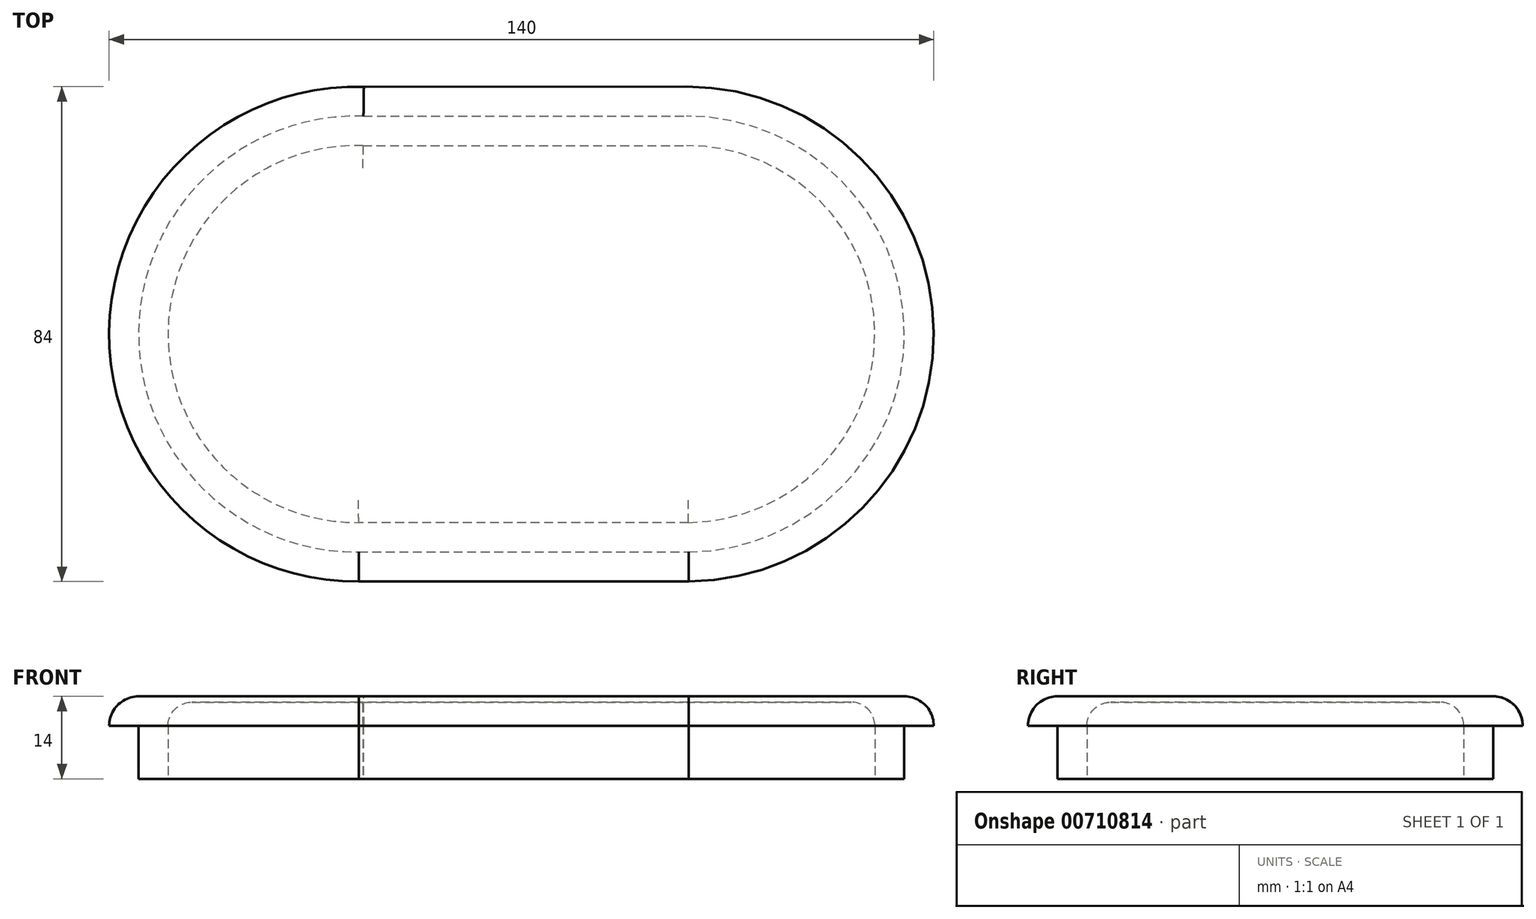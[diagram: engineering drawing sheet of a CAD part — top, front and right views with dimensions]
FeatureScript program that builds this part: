
annotation { "Feature Type Name" : "Feature", "Feature Type Description" : "" }
export const myFeature = defineFeature(function(context is Context, id is Id, definition is map)
    precondition{}
    {
        {
            var Q0;
            Q0=qCreatedBy(makeId("Top.planeOp"),FACE);
            var sketch = newSketch(context, id + "F0", { "sketchPlane" : qUnion([Q0])});
            skArc(sketch, "E0", {"start": v(-13.26, 36.98) * mm, "mid": v(-51.43, 0.4) * mm, "end": v(-14.05, -37) * mm});
            skArc(sketch, "E1", {"start": v(41.18, -37) * mm, "mid": v(78.56, -0.19) * mm, "end": v(41.55, 37) * mm});
            skLineSegment(sketch, "E2", {"start": v(-13.26, 36.98) * mm, "end": v(41.55, 37) * mm});
            skLineSegment(sketch, "E3", {"start": v(-14.05, -37) * mm, "end": v(41.95, -37) * mm});
            skSolve(sketch);
        }
        {
            var Q0;
            {var subQ1=sQuery(id+"F0.wireOp",EDGE,"E0");Q0=makeQuery(id+"F0.imprint","IMPRINT",FACE,{"disambiguationData":[TD([[makeQuery(id+"F0.imprint","IMPRINT",EDGE,{"derivedFrom":subQ1}),1.0]])]});}
            extrude(context, id + "F1", {"entities" : qUnion([Q0]), "depth" : 9 * mm, "offsetDistance" : 25 * mm});
        }
        {
            var Q0;
            Q0=makeQuery(id+"F1.opExtrude","CAP_FACE",FACE,{"disambiguationData":[OSD([sQuery(id+"F0.wireOp",EDGE,"E0"),sQuery(id+"F0.wireOp",EDGE,"E1"),sQuery(id+"F0.wireOp",EDGE,"E2"),sQuery(id+"F0.wireOp",EDGE,"E3")])],"isStart":false});
            var sketch = newSketch(context, id + "F2", { "sketchPlane" : qUnion([Q0])});
            skArc(sketch, "E4.0", {"start": v(-13.19, 41.98) * mm, "mid": v(-56.43, 0.42) * mm, "end": v(-14.02, -42) * mm});
            skLineSegment(sketch, "E4.1", {"start": v(-13.19, 41.98) * mm, "end": v(41.55, 42) * mm});
            skArc(sketch, "E4.2", {"start": v(41.98, -42) * mm, "mid": v(83.56, 0.21) * mm, "end": v(41.55, 42) * mm});
            skLineSegment(sketch, "E4.3", {"start": v(-14.02, -42) * mm, "end": v(41.98, -42) * mm});
            skSolve(sketch);
        }
        {
            var Q0;
            Q0=makeQuery(id+"F2.imprint","IMPRINT",FACE,{"disambiguationData":[TD([[makeQuery(id+"F2.imprint","IMPRINT",EDGE,{"derivedFrom":sQuery(id+"F2.wireOp",EDGE,"E4.0")}),1.0]])]});
            var Q1;
            Q1=makeQuery(id+"F2.imprint","IMPRINT",FACE,{"disambiguationData":[TD([[makeQuery(id+"F2.imprint","IMPRINT",EDGE,{"derivedFrom":makeQuery(id+"F1.opExtrude","CAP_EDGE",EDGE,{"disambiguationData":[OSD([sQuery(id+"F0.wireOp",EDGE,"E0")])],"isStart":false})}),1.0]])]});
            extrude(context, id + "F3", {"entities" : qUnion([Q0, Q1]), "operationType" : NewBodyOperationType.ADD, "depth" : 5 * mm, "offsetDistance" : 25 * mm});
        }
        {
            var Q0;
            Q0=makeQuery(id+"F3.opExtrude","CAP_EDGE",EDGE,{"disambiguationData":[OSD([sQuery(id+"F2.wireOp",EDGE,"E4.0")])],"isStart":false});
            var Q1;
            Q1=makeQuery(id+"F3.opExtrude","CAP_EDGE",EDGE,{"disambiguationData":[OSD([sQuery(id+"F2.wireOp",EDGE,"E4.1")])],"isStart":false});
            var Q2;
            Q2=makeQuery(id+"F3.opExtrude","CAP_EDGE",EDGE,{"disambiguationData":[OSD([sQuery(id+"F2.wireOp",EDGE,"E4.2")])],"isStart":false});
            fillet(context, id + "F4", {"entities" : qUnion([Q0, Q1, Q2]), "radius" : 5 * mm, "tangentPropagation" : true, "allowEdgeOverflow" : false});
        }
        {
            var Q0;
            Q0=makeQuery(id+"F1.opExtrude","CAP_FACE",FACE,{"disambiguationData":[OSD([sQuery(id+"F0.wireOp",EDGE,"E0"),sQuery(id+"F0.wireOp",EDGE,"E1"),sQuery(id+"F0.wireOp",EDGE,"E2"),sQuery(id+"F0.wireOp",EDGE,"E3")])],"isStart":true});
            var sketch = newSketch(context, id + "F5", { "sketchPlane" : qUnion([Q0])});
            skLineSegment(sketch, "E5.0", {"start": v(41.92, 32) * mm, "end": v(-14.08, 32) * mm});
            skArc(sketch, "E5.1", {"start": v(41.55, -32) * mm, "mid": v(73.56, -0.19) * mm, "end": v(41.92, 32) * mm});
            skLineSegment(sketch, "E5.2", {"start": v(-13.34, -31.98) * mm, "end": v(41.55, -32) * mm});
            skArc(sketch, "E5.3", {"start": v(-14.08, 32) * mm, "mid": v(-46.43, -0.37) * mm, "end": v(-13.34, -31.98) * mm});
            skSolve(sketch);
        }
        {
            var Q0;
            Q0=makeQuery(id+"F5.imprint","IMPRINT",FACE,{"disambiguationData":[TD([[makeQuery(id+"F5.imprint","IMPRINT",EDGE,{"derivedFrom":sQuery(id+"F5.wireOp",EDGE,"E5.0")}),1.0]])]});
            extrude(context, id + "F6", {"entities" : qUnion([Q0]), "operationType" : NewBodyOperationType.REMOVE, "oppositeDirection" : true, "depth" : 13 * mm, "offsetDistance" : 25 * mm});
        }
        {
            var Q0;
            Q0=makeQuery(id+"F6.boolean.opBoolean","COPY",EDGE,{"derivedFrom":makeQuery(id+"F6.opExtrude","CAP_EDGE",EDGE,{"disambiguationData":[OSD([sQuery(id+"F5.wireOp",EDGE,"E5.3")])],"isStart":false})});
            var Q1;
            Q1=makeQuery(id+"F6.boolean.opBoolean","COPY",FACE,{"derivedFrom":makeQuery(id+"F6.opExtrude","CAP_FACE",FACE,{"disambiguationData":[OSD([sQuery(id+"F5.wireOp",EDGE,"E5.0"),sQuery(id+"F5.wireOp",EDGE,"E5.1"),sQuery(id+"F5.wireOp",EDGE,"E5.2"),sQuery(id+"F5.wireOp",EDGE,"E5.3")])],"isStart":false})});
            fillet(context, id + "F7", {"entities" : qUnion([Q0, Q1]), "radius" : 4 * mm, "tangentPropagation" : true, "allowEdgeOverflow" : false});
        }
    });
